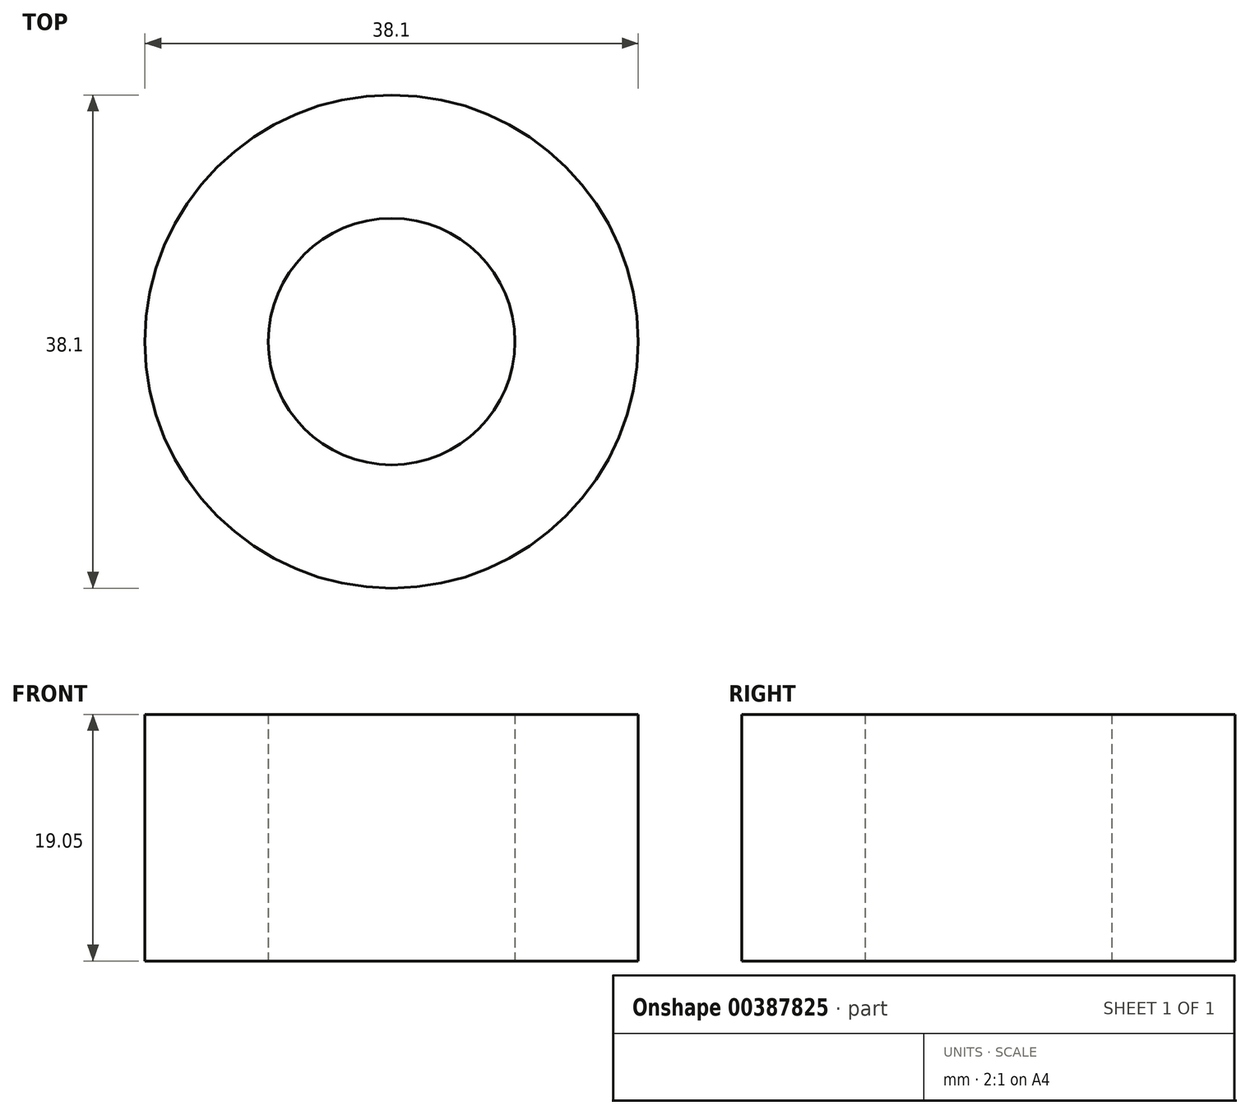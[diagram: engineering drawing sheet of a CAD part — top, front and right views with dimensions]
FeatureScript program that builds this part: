
annotation { "Feature Type Name" : "Feature", "Feature Type Description" : "" }
export const myFeature = defineFeature(function(context is Context, id is Id, definition is map)
    precondition{}
    {
        {
            var Q0;
            Q0=qCreatedBy(makeId("Top.planeOp"),FACE);
            var sketch = newSketch(context, id + "F0", { "sketchPlane" : qUnion([Q0])});
            skCircle(sketch, "E0", {"center": v(0, 0) * mm, "radius": 19.05 * mm});
            skCircle(sketch, "E1", {"center": v(0, 0) * mm, "radius": 9.53 * mm});
            skSolve(sketch);
        }
        {
            var Q0;
            Q0=makeQuery(id+"F0.imprint","IMPRINT",FACE,{"disambiguationData":[TD([[makeQuery(id+"F0.imprint","IMPRINT",EDGE,{"derivedFrom":sQuery(id+"F0.wireOp",EDGE,"E0")}),1.0]])]});
            extrude(context, id + "F1", {"entities" : qUnion([Q0]), "depth" : 19.05 * mm});
        }
    });
